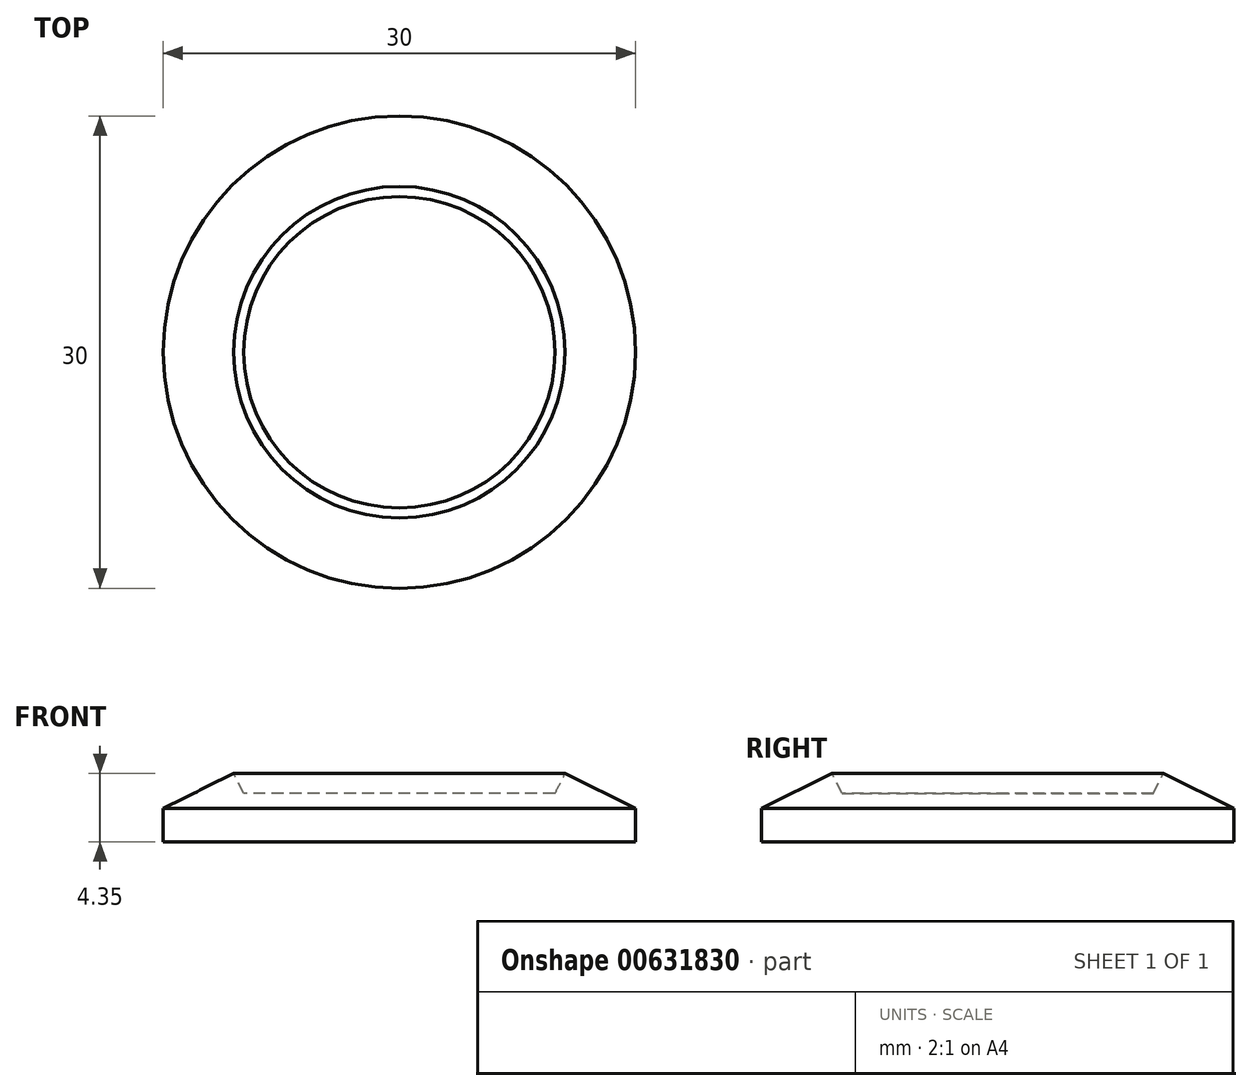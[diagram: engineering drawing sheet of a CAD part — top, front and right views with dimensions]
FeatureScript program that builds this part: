
annotation { "Feature Type Name" : "Feature", "Feature Type Description" : "" }
export const myFeature = defineFeature(function(context is Context, id is Id, definition is map)
    precondition{}
    {
        {
            var Q0;
            Q0=qCreatedBy(makeId("Front.planeOp"),FACE);
            var sketch = newSketch(context, id + "F0", { "sketchPlane" : qUnion([Q0])});
            skLineSegment(sketch, "E0", {"start": v(0, 9.59) * mm, "end": v(0, -2.57) * mm, "construction": true});
            skLineSegment(sketch, "E1", {"start": v(0, 8.62) * mm, "end": v(15, 1.12) * mm, "construction": true});
            skLineSegment(sketch, "E2", {"start": v(0, -1) * mm, "end": v(13.94, -1) * mm});
            skLineSegment(sketch, "E3", {"start": v(13.94, -1) * mm, "end": v(15.45, 2.01) * mm});
            skLineSegment(sketch, "E4", {"start": v(15.45, 2.01) * mm, "end": v(10.84, 3.98) * mm});
            skLineSegment(sketch, "E5", {"start": v(10.84, 3.98) * mm, "end": v(9.89, 2.07) * mm});
            skLineSegment(sketch, "E6", {"start": v(9.89, 2.07) * mm, "end": v(0, 2.07) * mm});
            skPoint(sketch, "E7", {"position": v(14.44, 0) * mm});
            skPoint(sketch, "E8", {"position": v(15, 1.12) * mm});
            skPoint(sketch, "E9", {"position": v(10.14, 2.57) * mm});
            skLineSegment(sketch, "E10", {"start": v(0, 8.62) * mm, "end": v(15.45, 2.01) * mm, "construction": true});
            skLineSegment(sketch, "E11", {"start": v(0, 8.62) * mm, "end": v(14.44, 0) * mm, "construction": true});
            skPoint(sketch, "E12", {"position": v(10.53, 3.35) * mm});
            skLineSegment(sketch, "E13", {"start": v(0, 2.07) * mm, "end": v(0, -1) * mm});
            skSolve(sketch);
        }
        {
            var Q0;
            Q0=qCreatedBy(makeId("Front.planeOp"),FACE);
            var sketch = newSketch(context, id + "F1", { "sketchPlane" : qUnion([Q0])});
            skLineSegment(sketch, "E14.0", {"start": v(9.89, 2.07) * mm, "end": v(0, 2.07) * mm});
            skLineSegment(sketch, "E15.0", {"start": v(10.53, 3.35) * mm, "end": v(9.89, 2.07) * mm});
            skLineSegment(sketch, "E16.0", {"start": v(10.53, 3.35) * mm, "end": v(15, 1.12) * mm});
            skLineSegment(sketch, "E17.0", {"start": v(13.94, -1) * mm, "end": v(15, 1.12) * mm});
            skLineSegment(sketch, "E18.0", {"start": v(0, -1) * mm, "end": v(13.94, -1) * mm});
            skPoint(sketch, "E19.orphan", {"position": v(0, 8.62) * mm});
            skPoint(sketch, "E20.orphan", {"position": v(15.45, 2.01) * mm});
            skLineSegment(sketch, "E21.0", {"start": v(0, 2.07) * mm, "end": v(0, -1) * mm});
            skSolve(sketch);
        }
        {
            var Q0;
            Q0=qSketchRegion(id+"F1",true);
            var Q1;
            Q1=sQuery(id+"F0.wireOp",EDGE,"E0");
            revolve(context, id + "F2", {"entities" : qUnion([Q0]), "axis" : qUnion([Q1]), "revolveType" : RevolveType.FULL});
        }
        {
            var Q0;
            Q0=makeQuery(id+"F2.opRevolve","SWEPT_FACE",FACE,{"disambiguationData":[OSD([sQuery(id+"F1.wireOp",EDGE,"E18.0")])]});
            var sketch = newSketch(context, id + "F3", { "sketchPlane" : qUnion([Q0])});
            skCircle(sketch, "E22.0", {"center": v(0, 0) * mm, "radius": 15 * mm});
            skCircle(sketch, "E23.0", {"center": v(0, 0) * mm, "radius": 13.94 * mm});
            skSolve(sketch);
        }
        {
            var Q0;
            Q0 = qSketchRegion(id + "F3", true);
            extrude(context, id + "F4", {"entities" : qUnion([Q0]), "operationType" : NewBodyOperationType.ADD, "endBound" : BoundingType.UP_TO_NEXT, "oppositeDirection" : true, "depth" : 25 * mm, "offsetDistance" : 25 * mm});
        }
    });
